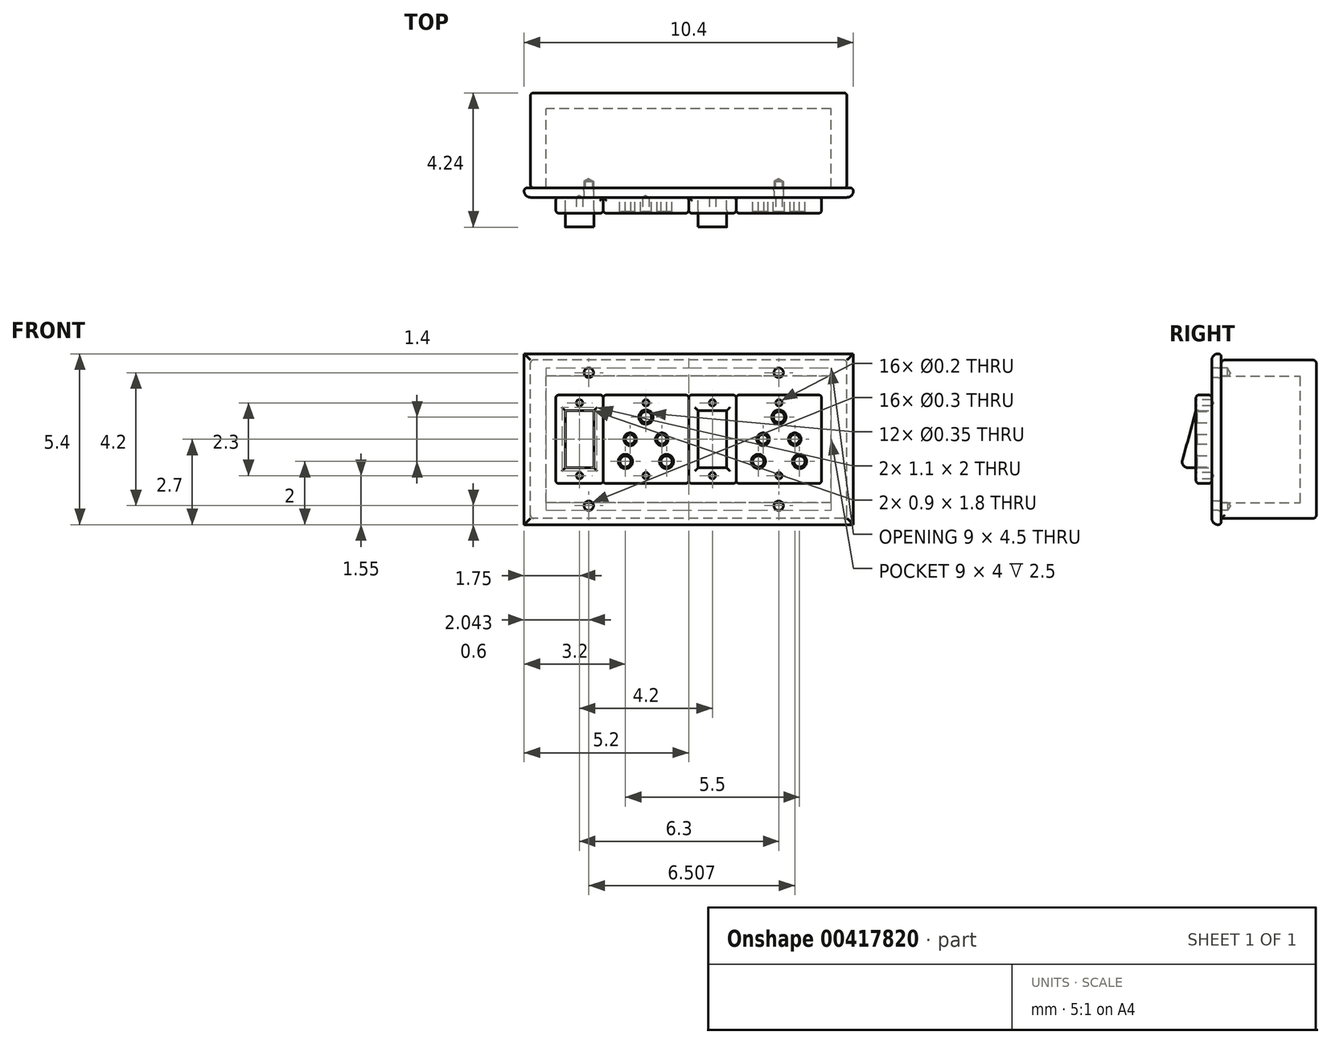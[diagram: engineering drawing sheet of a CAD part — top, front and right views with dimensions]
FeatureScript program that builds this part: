
annotation { "Feature Type Name" : "Feature", "Feature Type Description" : "" }
export const myFeature = defineFeature(function(context is Context, id is Id, definition is map)
    precondition{}
    {
        {
            var Q0;
            Q0=qCreatedBy(makeId("Front.planeOp"),FACE);
            var sketch = newSketch(context, id + "F0", { "sketchPlane" : qUnion([Q0])});
            skLineSegment(sketch, "E0.bottom", {"start": v(5, -2.5) * mm, "end": v(-5, -2.5) * mm});
            skLineSegment(sketch, "E0.top", {"start": v(5, 2.5) * mm, "end": v(-5, 2.5) * mm});
            skLineSegment(sketch, "E0.left", {"start": v(5, -2.5) * mm, "end": v(5, 2.5) * mm});
            skLineSegment(sketch, "E0.right", {"start": v(-5, -2.5) * mm, "end": v(-5, 2.5) * mm});
            skPoint(sketch, "E0.middle", {"position": v(0, 0) * mm});
            skSolve(sketch);
        }
        {
            var Q0;
            Q0=makeQuery(id+"F0.imprint","IMPRINT",FACE,{"disambiguationData":[TD([[makeQuery(id+"F0.imprint","IMPRINT",EDGE,{"derivedFrom":sQuery(id+"F0.wireOp",EDGE,"E0.bottom")}),-1.0]])]});
            extrude(context, id + "F1", {"entities" : qUnion([Q0]), "depth" : 3 * mm});
        }
        {
            var Q0;
            Q0=makeQuery(id+"F1.opExtrude","CAP_FACE",FACE,{"disambiguationData":[OSD([sQuery(id+"F0.wireOp",EDGE,"E0.bottom"),sQuery(id+"F0.wireOp",EDGE,"E0.top"),sQuery(id+"F0.wireOp",EDGE,"E0.left"),sQuery(id+"F0.wireOp",EDGE,"E0.right")])],"isStart":false});
            shell(context, id + "F2", {"entities" : qUnion([Q0]), "thickness" : 0.5 * mm});
        }
        {
            var Q0;
            Q0=makeQuery(id+"F1.opExtrude","CAP_FACE",FACE,{"disambiguationData":[OSD([sQuery(id+"F0.wireOp",EDGE,"E0.bottom"),sQuery(id+"F0.wireOp",EDGE,"E0.top"),sQuery(id+"F0.wireOp",EDGE,"E0.left"),sQuery(id+"F0.wireOp",EDGE,"E0.right")])],"isStart":false});
            var sketch = newSketch(context, id + "F3", { "sketchPlane" : qUnion([Q0])});
            skLineSegment(sketch, "E1.bottom", {"start": v(5.2, -2.7) * mm, "end": v(-5.2, -2.7) * mm});
            skLineSegment(sketch, "E1.top", {"start": v(5.2, 2.7) * mm, "end": v(-5.2, 2.7) * mm});
            skLineSegment(sketch, "E1.left", {"start": v(5.2, -2.7) * mm, "end": v(5.2, 2.7) * mm});
            skLineSegment(sketch, "E1.right", {"start": v(-5.2, -2.7) * mm, "end": v(-5.2, 2.7) * mm});
            skPoint(sketch, "E1.middle", {"position": v(0, 0) * mm});
            skSolve(sketch);
        }
        {
            var Q0;
            Q0=makeQuery(id+"F3.imprint","IMPRINT",FACE,{"disambiguationData":[TD([[makeQuery(id+"F3.imprint","IMPRINT",EDGE,{"derivedFrom":sQuery(id+"F3.wireOp",EDGE,"E1.bottom")}),-1.0]])]});
            var Q1;
            {var subQ0=sQuery(id+"F0.wireOp",EDGE,"E0.bottom");Q1=makeQuery(id+"F3.imprint","IMPRINT",FACE,{"disambiguationData":[TD([[makeQuery(id+"F3.imprint","IMPRINT",EDGE,{"derivedFrom":makeQuery(id+"F2.opShell","OFFSET_EDGE",EDGE,{"disambiguationData":[OSD([subQ0]),TDD([makeQuery(id+"F1.opExtrude","CAP_EDGE",EDGE,{"disambiguationData":[OSD([subQ0])],"isStart":false})])]})}),-1.0]])]});}
            var Q2;
            {var subQ6=sQuery(id+"F0.wireOp",EDGE,"E0.bottom");var subQ7=makeQuery(id+"F1.opExtrude","CAP_EDGE",EDGE,{"disambiguationData":[OSD([subQ6])],"isStart":false});Q2=makeQuery(id+"F3.imprint","IMPRINT",FACE,{"disambiguationData":[TD([[makeQuery(id+"F3.imprint","IMPRINT",EDGE,{"derivedFrom":subQ7}),-1.0]])]});}
            extrude(context, id + "F4", {"entities" : qUnion([Q0, Q1, Q2]), "depth" : 0.3 * mm});
        }
        {
            var Q0;
            Q0=makeQuery(id+"F4.opExtrude","CAP_FACE",FACE,{"disambiguationData":[OSD([sQuery(id+"F3.wireOp",EDGE,"E1.bottom"),sQuery(id+"F3.wireOp",EDGE,"E1.top"),sQuery(id+"F3.wireOp",EDGE,"E1.left"),sQuery(id+"F3.wireOp",EDGE,"E1.right")])],"isStart":false});
            var sketch = newSketch(context, id + "F5", { "sketchPlane" : qUnion([Q0])});
            skLineSegment(sketch, "E2.bottom", {"start": v(-2.7, -1.4) * mm, "end": v(-4.2, -1.4) * mm});
            skLineSegment(sketch, "E2.top", {"start": v(-2.7, 1.4) * mm, "end": v(-4.2, 1.4) * mm});
            skLineSegment(sketch, "E2.left", {"start": v(-2.7, -1.4) * mm, "end": v(-2.7, 1.4) * mm});
            skLineSegment(sketch, "E2.right", {"start": v(-4.2, -1.4) * mm, "end": v(-4.2, 1.4) * mm});
            skPoint(sketch, "E2.middle", {"position": v(-3.45, 0) * mm});
            skLineSegment(sketch, "E3.bottom", {"start": v(0, -1.4) * mm, "end": v(-2.7, -1.4) * mm});
            skLineSegment(sketch, "E3.top", {"start": v(0, 1.4) * mm, "end": v(-2.7, 1.4) * mm});
            skLineSegment(sketch, "E3.left", {"start": v(0, -1.4) * mm, "end": v(0, 1.4) * mm});
            skPoint(sketch, "E3.middle", {"position": v(-1.35, 0) * mm});
            skLineSegment(sketch, "E4.bottom", {"start": v(-3, -0.9) * mm, "end": v(-3.9, -0.9) * mm});
            skLineSegment(sketch, "E4.top", {"start": v(-3, 0.9) * mm, "end": v(-3.9, 0.9) * mm});
            skLineSegment(sketch, "E4.left", {"start": v(-3, -0.9) * mm, "end": v(-3, 0.9) * mm});
            skLineSegment(sketch, "E4.right", {"start": v(-3.9, -0.9) * mm, "end": v(-3.9, 0.9) * mm});
            skCircle(sketch, "E5", {"center": v(-1.35, 0.7) * mm, "radius": 0.17 * mm});
            skCircle(sketch, "E6", {"center": v(-1.85, 0) * mm, "radius": 0.15 * mm});
            skCircle(sketch, "E7", {"center": v(-0.85, 0) * mm, "radius": 0.15 * mm});
            skCircle(sketch, "E8", {"center": v(-2, -0.7) * mm, "radius": 0.17 * mm});
            skCircle(sketch, "E9", {"center": v(-0.7, -0.7) * mm, "radius": 0.17 * mm});
            skPoint(sketch, "E10", {"position": v(-3.45, 1.15) * mm});
            skPoint(sketch, "E11", {"position": v(-1.35, 1.15) * mm});
            skPoint(sketch, "E12", {"position": v(-1.35, -1.15) * mm});
            skPoint(sketch, "E13", {"position": v(-3.45, -1.15) * mm});
            skSolve(sketch);
        }
        {
            var Q0;
            Q0=makeQuery(id+"F5.imprint","IMPRINT",FACE,{"disambiguationData":[TD([[makeQuery(id+"F5.imprint","IMPRINT",EDGE,{"derivedFrom":sQuery(id+"F5.wireOp",EDGE,"E2.bottom")}),-1.0]])]});
            extrude(context, id + "F6", {"entities" : qUnion([Q0]), "depth" : 0.5 * mm});
        }
        {
            var Q0;
            Q0=makeQuery(id+"F5.imprint","IMPRINT",FACE,{"disambiguationData":[TD([[makeQuery(id+"F5.imprint","IMPRINT",EDGE,{"derivedFrom":sQuery(id+"F5.wireOp",EDGE,"E3.bottom")}),-1.0]])]});
            extrude(context, id + "F7", {"entities" : qUnion([Q0]), "depth" : 0.5 * mm});
        }
        {
            var Q0;
            Q0=makeQuery(id+"F6.opExtrude","SWEPT_FACE",FACE,{"disambiguationData":[OSD([sQuery(id+"F5.wireOp",EDGE,"E4.right")])]});
            var sketch = newSketch(context, id + "F8", { "sketchPlane" : qUnion([Q0])});
            skLineSegment(sketch, "E14.0.0", {"start": v(-3.3, -2.7) * mm, "end": v(-3.3, 2.7) * mm});
            skLineSegment(sketch, "E14.0.2", {"start": v(-3.3, 2.7) * mm, "end": v(-3.3, -2.7) * mm});
            skPoint(sketch, "E15.0", {"position": v(-3.8, -0.9) * mm});
            skPoint(sketch, "E16.0", {"position": v(-3.8, 0.9) * mm});
            skLineSegment(sketch, "E17", {"start": v(-3.8, 0.9) * mm, "end": v(-3.8, -0.9) * mm});
            skLineSegment(sketch, "E18", {"start": v(-4.05, -0.9) * mm, "end": v(-3.8, -0.9) * mm});
            skArc(sketch, "E19", {"start": v(-4.23, -0.66) * mm, "mid": v(-4.01, 0.12) * mm, "end": v(-3.8, 0.9) * mm});
            skPoint(sketch, "E20.visualSharp", {"position": v(-4.3, -0.9) * mm});
            skArc(sketch, "E20.filletArc", {"start": v(-4.23, -0.66) * mm, "mid": v(-4.2, -0.82) * mm, "end": v(-4.05, -0.9) * mm});
            skSolve(sketch);
        }
        {
            var Q0;
            Q0=makeQuery(id+"F8.imprint","IMPRINT",FACE,{"disambiguationData":[TD([[makeQuery(id+"F8.imprint","IMPRINT",EDGE,{"derivedFrom":sQuery(id+"F8.wireOp",EDGE,"E17")}),1.0]])]});
            var Q1;
            Q1=makeQuery(id+"F6.opExtrude","SWEPT_FACE",FACE,{"disambiguationData":[OSD([sQuery(id+"F5.wireOp",EDGE,"E4.left")])]});
            extrude(context, id + "F9", {"entities" : qUnion([Q0]), "endBound" : BoundingType.UP_TO_SURFACE, "endBoundEntityFace" : qUnion([Q1]), "depth" : 25 * mm});
        }
        {
            var Q0;
            Q0=makeQuery(id+"F6.opExtrude","CAP_FACE",FACE,{"disambiguationData":[OSD([sQuery(id+"F5.wireOp",EDGE,"E2.bottom"),sQuery(id+"F5.wireOp",EDGE,"E2.top"),sQuery(id+"F5.wireOp",EDGE,"E2.right"),sQuery(id+"F5.wireOp",EDGE,"E2.left"),sQuery(id+"F5.wireOp",EDGE,"E4.bottom"),sQuery(id+"F5.wireOp",EDGE,"E4.top"),sQuery(id+"F5.wireOp",EDGE,"E4.left"),sQuery(id+"F5.wireOp",EDGE,"E4.right")])],"isStart":false});
            var Q1;
            Q1=makeQuery(id+"F6.opExtrude","SWEPT_EDGE",EDGE,{"disambiguationData":[OSD([sQuery(id+"F5.wireOp",EDGE,"E2.top"),sQuery(id+"F5.wireOp",EDGE,"E2.right")])]});
            var Q2;
            Q2=makeQuery(id+"F6.opExtrude","SWEPT_EDGE",EDGE,{"disambiguationData":[OSD([sQuery(id+"F5.wireOp",EDGE,"E2.bottom"),sQuery(id+"F5.wireOp",EDGE,"E2.right")])]});
            var Q3;
            Q3=makeQuery(id+"F6.opExtrude","CAP_EDGE",EDGE,{"disambiguationData":[OSD([sQuery(id+"F5.wireOp",EDGE,"E2.right")])],"isStart":true});
            var Q4;
            Q4=makeQuery(id+"F6.opExtrude","CAP_EDGE",EDGE,{"disambiguationData":[OSD([sQuery(id+"F5.wireOp",EDGE,"E2.top")])],"isStart":true});
            var Q5;
            Q5=makeQuery(id+"F6.opExtrude","CAP_EDGE",EDGE,{"disambiguationData":[OSD([sQuery(id+"F5.wireOp",EDGE,"E2.bottom")])],"isStart":true});
            var Q6;
            Q6=makeQuery(id+"F6.opExtrude","SWEPT_EDGE",EDGE,{"disambiguationData":[OSD([sQuery(id+"F5.wireOp",EDGE,"E2.top"),sQuery(id+"F5.wireOp",EDGE,"E3.top"),sQuery(id+"F5.wireOp",EDGE,"E2.left")])]});
            var Q7;
            Q7=makeQuery(id+"F6.opExtrude","SWEPT_EDGE",EDGE,{"disambiguationData":[OSD([sQuery(id+"F5.wireOp",EDGE,"E2.bottom"),sQuery(id+"F5.wireOp",EDGE,"E3.bottom"),sQuery(id+"F5.wireOp",EDGE,"E2.left")])]});
            fillet(context, id + "F10", {"entities" : qUnion([Q0, Q1, Q2, Q3, Q4, Q5, Q6, Q7]), "radius" : 0.1 * mm, "tangentPropagation" : true, "allowEdgeOverflow" : false});
        }
        {
            var Q0;
            Q0=makeQuery(id+"F7.opExtrude","CAP_EDGE",EDGE,{"disambiguationData":[OSD([sQuery(id+"F5.wireOp",EDGE,"E5")])],"isStart":false});
            var Q1;
            Q1=makeQuery(id+"F7.opExtrude","CAP_EDGE",EDGE,{"disambiguationData":[OSD([sQuery(id+"F5.wireOp",EDGE,"E6")])],"isStart":false});
            var Q2;
            Q2=makeQuery(id+"F7.opExtrude","CAP_EDGE",EDGE,{"disambiguationData":[OSD([sQuery(id+"F5.wireOp",EDGE,"E7")])],"isStart":false});
            var Q3;
            Q3=makeQuery(id+"F7.opExtrude","CAP_EDGE",EDGE,{"disambiguationData":[OSD([sQuery(id+"F5.wireOp",EDGE,"E8")])],"isStart":false});
            var Q4;
            Q4=makeQuery(id+"F7.opExtrude","CAP_EDGE",EDGE,{"disambiguationData":[OSD([sQuery(id+"F5.wireOp",EDGE,"E9")])],"isStart":false});
            chamfer(context, id + "F11", {"entities" : qUnion([Q0, Q1, Q2, Q3, Q4]), "width" : 0.05 * mm, "tangentPropagation" : true});
        }
        {
            var Q0;
            Q0=makeQuery(id+"F7.opExtrude","SWEPT_FACE",FACE,{"disambiguationData":[OSD([sQuery(id+"F5.wireOp",EDGE,"E3.top")])]});
            var Q1;
            Q1=makeQuery(id+"F7.opExtrude","SWEPT_FACE",FACE,{"disambiguationData":[OSD([sQuery(id+"F5.wireOp",EDGE,"E3.left")])]});
            var Q2;
            Q2=makeQuery(id+"F7.opExtrude","SWEPT_FACE",FACE,{"disambiguationData":[OSD([sQuery(id+"F5.wireOp",EDGE,"E3.bottom")])]});
            fillet(context, id + "F12", {"entities" : qUnion([Q0, Q1, Q2]), "radius" : 0.1 * mm, "tangentPropagation" : true, "allowEdgeOverflow" : false});
        }
        {
            var Q0;
            Q0=makeQuery(id+"F4.opExtrude","CAP_FACE",FACE,{"disambiguationData":[OSD([sQuery(id+"F3.wireOp",EDGE,"E1.bottom"),sQuery(id+"F3.wireOp",EDGE,"E1.top"),sQuery(id+"F3.wireOp",EDGE,"E1.left"),sQuery(id+"F3.wireOp",EDGE,"E1.right")])],"isStart":false});
            fillet(context, id + "F13", {"entities" : qUnion([Q0]), "radius" : 0.2 * mm, "tangentPropagation" : true, "allowEdgeOverflow" : false});
        }
        {
            var Q0;
            Q0=makeQuery(id+"F6.opExtrude","CAP_FACE",FACE,{"disambiguationData":[OSD([sQuery(id+"F5.wireOp",EDGE,"E2.bottom"),sQuery(id+"F5.wireOp",EDGE,"E2.top"),sQuery(id+"F5.wireOp",EDGE,"E2.right"),sQuery(id+"F5.wireOp",EDGE,"E2.left"),sQuery(id+"F5.wireOp",EDGE,"E4.bottom"),sQuery(id+"F5.wireOp",EDGE,"E4.top"),sQuery(id+"F5.wireOp",EDGE,"E4.left"),sQuery(id+"F5.wireOp",EDGE,"E4.right")])],"isStart":false});
            var sketch = newSketch(context, id + "F14", { "sketchPlane" : qUnion([Q0])});
            skPoint(sketch, "E21.0", {"position": v(-3.45, 1.15) * mm});
            skPoint(sketch, "E22.0", {"position": v(-3.45, -1.15) * mm});
            skPoint(sketch, "E23.0", {"position": v(-1.35, 1.15) * mm});
            skPoint(sketch, "E24.0", {"position": v(-1.35, -1.15) * mm});
            skSolve(sketch);
        }
        {
            var Q0;
            Q0=sQuery(id+"F14.wireOp",VERTEX,"E21.0");
            var Q1;
            Q1=sQuery(id+"F14.wireOp",VERTEX,"E23.0");
            var Q2;
            Q2=sQuery(id+"F14.wireOp",VERTEX,"E22.0");
            var Q3;
            Q3=sQuery(id+"F14.wireOp",VERTEX,"E24.0");
            var Q4;
            Q4=makeQuery(id+"F4.opExtrude","SWEPT_BODY",BODY,{"disambiguationData":[OSD([sQuery(id+"F3.wireOp",EDGE,"E1.bottom"),sQuery(id+"F3.wireOp",EDGE,"E1.top"),sQuery(id+"F3.wireOp",EDGE,"E1.left"),sQuery(id+"F3.wireOp",EDGE,"E1.right")])]});
            var Q5;
            Q5=makeQuery(id+"F6.opExtrude","SWEPT_BODY",BODY,{"disambiguationData":[OSD([sQuery(id+"F5.wireOp",EDGE,"E2.bottom"),sQuery(id+"F5.wireOp",EDGE,"E2.top"),sQuery(id+"F5.wireOp",EDGE,"E2.right"),sQuery(id+"F5.wireOp",EDGE,"E2.left"),sQuery(id+"F5.wireOp",EDGE,"E4.bottom"),sQuery(id+"F5.wireOp",EDGE,"E4.top"),sQuery(id+"F5.wireOp",EDGE,"E4.left"),sQuery(id+"F5.wireOp",EDGE,"E4.right")])]});
            var Q6;
            Q6=makeQuery(id+"F7.opExtrude","SWEPT_BODY",BODY,{"disambiguationData":[OSD([sQuery(id+"F5.wireOp",EDGE,"E3.bottom"),sQuery(id+"F5.wireOp",EDGE,"E3.top"),sQuery(id+"F5.wireOp",EDGE,"E3.left"),sQuery(id+"F5.wireOp",EDGE,"E2.left"),sQuery(id+"F5.wireOp",EDGE,"E5"),sQuery(id+"F5.wireOp",EDGE,"E6"),sQuery(id+"F5.wireOp",EDGE,"E7"),sQuery(id+"F5.wireOp",EDGE,"E8"),sQuery(id+"F5.wireOp",EDGE,"E9")])]});
            hole(context, id + "F15", {"style" : HoleStyle.SIMPLE, "endStyle" : HoleEndStyle.BLIND, "holeDiameter" : 0.2 * mm, "holeDepth" : 0.5 * mm, "isTappedThrough" : true, "tappedDepth" : 19.25 * mm, "tapClearance" : 3, "startFromSketch" : true, "locations" : qUnion([Q0, Q1, Q2, Q3]), "scope" : qUnion([Q4, Q5, Q6])});
        }
        {
            var Q0;
            Q0=makeQuery(id+"F4.opExtrude","CAP_FACE",FACE,{"disambiguationData":[OSD([sQuery(id+"F3.wireOp",EDGE,"E1.bottom"),sQuery(id+"F3.wireOp",EDGE,"E1.top"),sQuery(id+"F3.wireOp",EDGE,"E1.left"),sQuery(id+"F3.wireOp",EDGE,"E1.right")])],"isStart":false});
            var sketch = newSketch(context, id + "F16", { "sketchPlane" : qUnion([Q0])});
            skPoint(sketch, "E25", {"position": v(-3.16, 2.1) * mm});
            skPoint(sketch, "E26", {"position": v(2.84, 2.1) * mm});
            skPoint(sketch, "E27", {"position": v(-3.16, -2.1) * mm});
            skPoint(sketch, "E28", {"position": v(2.84, -2.1) * mm});
            skSolve(sketch);
        }
        {
            var Q0;
            Q0=sQuery(id+"F16.wireOp",VERTEX,"E25");
            var Q1;
            Q1=sQuery(id+"F16.wireOp",VERTEX,"E26");
            var Q2;
            Q2=sQuery(id+"F16.wireOp",VERTEX,"E27");
            var Q3;
            Q3=sQuery(id+"F16.wireOp",VERTEX,"E28");
            var Q4;
            Q4=makeQuery(id+"F4.opExtrude","SWEPT_BODY",BODY,{"disambiguationData":[OSD([sQuery(id+"F3.wireOp",EDGE,"E1.bottom"),sQuery(id+"F3.wireOp",EDGE,"E1.top"),sQuery(id+"F3.wireOp",EDGE,"E1.left"),sQuery(id+"F3.wireOp",EDGE,"E1.right")])]});
            var Q5;
            Q5=makeQuery(id+"F1.opExtrude","SWEPT_BODY",BODY,{"disambiguationData":[OSD([sQuery(id+"F0.wireOp",EDGE,"E0.bottom"),sQuery(id+"F0.wireOp",EDGE,"E0.top"),sQuery(id+"F0.wireOp",EDGE,"E0.left"),sQuery(id+"F0.wireOp",EDGE,"E0.right")])]});
            hole(context, id + "F17", {"style" : HoleStyle.SIMPLE, "endStyle" : HoleEndStyle.BLIND, "holeDiameter" : 0.3 * mm, "holeDepth" : 0.5 * mm, "isTappedThrough" : true, "tappedDepth" : 19.25 * mm, "tapClearance" : 3, "startFromSketch" : true, "locations" : qUnion([Q0, Q1, Q2, Q3]), "scope" : qUnion([Q4, Q5])});
        }
        {
            var Q0;
            Q0=qCreatedBy(makeId("Right.planeOp"),FACE);
            cPlane(context, id + "F18", {"entities" : qUnion([Q0]), "cplaneType" : CPlaneType.OFFSET, "offset" : (2.7 / 2) * mm, "oppositeDirection" : true, "width" : 150 * mm, "height" : 150 * mm});
        }
        {
            var Q0;
            Q0=makeQuery(id+"F6.opExtrude","SWEPT_BODY",BODY,{"disambiguationData":[OSD([sQuery(id+"F5.wireOp",EDGE,"E2.bottom"),sQuery(id+"F5.wireOp",EDGE,"E2.top"),sQuery(id+"F5.wireOp",EDGE,"E2.right"),sQuery(id+"F5.wireOp",EDGE,"E2.left"),sQuery(id+"F5.wireOp",EDGE,"E4.bottom"),sQuery(id+"F5.wireOp",EDGE,"E4.top"),sQuery(id+"F5.wireOp",EDGE,"E4.left"),sQuery(id+"F5.wireOp",EDGE,"E4.right")])]});
            var Q1;
            Q1=makeQuery(id+"F9.opExtrude","SWEPT_BODY",BODY,{"disambiguationData":[OSD([sQuery(id+"F8.wireOp",EDGE,"E17"),sQuery(id+"F8.wireOp",EDGE,"E18"),sQuery(id+"F8.wireOp",EDGE,"E19"),sQuery(id+"F8.wireOp",EDGE,"E20.filletArc")])]});
            var Q2;
            Q2=qCreatedBy(id+"F18.planeOp",FACE);
            mirror(context, id + "F19", {"entities" : qUnion([Q0, Q1]), "mirrorPlane" : qUnion([Q2])});
        }
        {
            var Q0;
            Q0=qCreatedBy(makeId("Right.planeOp"),FACE);
            cPlane(context, id + "F20", {"entities" : qUnion([Q0]), "cplaneType" : CPlaneType.OFFSET, "offset" : (1.5 / 2) * mm, "width" : 150 * mm, "height" : 150 * mm});
        }
        {
            var Q0;
            Q0=makeQuery(id+"F7.opExtrude","SWEPT_BODY",BODY,{"disambiguationData":[OSD([sQuery(id+"F5.wireOp",EDGE,"E3.bottom"),sQuery(id+"F5.wireOp",EDGE,"E3.top"),sQuery(id+"F5.wireOp",EDGE,"E3.left"),sQuery(id+"F5.wireOp",EDGE,"E2.left"),sQuery(id+"F5.wireOp",EDGE,"E5"),sQuery(id+"F5.wireOp",EDGE,"E6"),sQuery(id+"F5.wireOp",EDGE,"E7"),sQuery(id+"F5.wireOp",EDGE,"E8"),sQuery(id+"F5.wireOp",EDGE,"E9")])]});
            var Q1;
            Q1=qCreatedBy(id+"F20.planeOp",FACE);
            mirror(context, id + "F21", {"entities" : qUnion([Q0]), "mirrorPlane" : qUnion([Q1])});
        }
        {
            var Q0;
            Q0=makeQuery(id+"F21.opPattern","COPY",FACE,{"derivedFrom":makeQuery(id+"F7.opExtrude","SWEPT_FACE",FACE,{"disambiguationData":[OSD([sQuery(id+"F5.wireOp",EDGE,"E2.left")])]}),"instanceName":"1"});
            var Q1;
            Q1=makeQuery(id+"F7.opExtrude","CAP_EDGE",EDGE,{"disambiguationData":[OSD([sQuery(id+"F5.wireOp",EDGE,"E2.left")])],"isStart":false});
            fillet(context, id + "F22", {"entities" : qUnion([Q0, Q1]), "radius" : 0.1 * mm, "tangentPropagation" : true, "allowEdgeOverflow" : false});
        }
        {
            var Q0;
            Q0=makeQuery(id+"F4.opExtrude","CAP_FACE",FACE,{"disambiguationData":[OSD([sQuery(id+"F3.wireOp",EDGE,"E1.bottom"),sQuery(id+"F3.wireOp",EDGE,"E1.top"),sQuery(id+"F3.wireOp",EDGE,"E1.left"),sQuery(id+"F3.wireOp",EDGE,"E1.right")])],"isStart":true});
            var Q1;
            Q1=makeQuery(id+"F1.opExtrude","SWEPT_FACE",FACE,{"disambiguationData":[OSD([sQuery(id+"F0.wireOp",EDGE,"E0.left")])]});
            var Q2;
            Q2=makeQuery(id+"F1.opExtrude","SWEPT_FACE",FACE,{"disambiguationData":[OSD([sQuery(id+"F0.wireOp",EDGE,"E0.top")])]});
            var Q3;
            Q3=makeQuery(id+"F1.opExtrude","CAP_FACE",FACE,{"disambiguationData":[OSD([sQuery(id+"F0.wireOp",EDGE,"E0.bottom"),sQuery(id+"F0.wireOp",EDGE,"E0.top"),sQuery(id+"F0.wireOp",EDGE,"E0.left"),sQuery(id+"F0.wireOp",EDGE,"E0.right")])],"isStart":true});
            var Q4;
            Q4=makeQuery(id+"F1.opExtrude","SWEPT_FACE",FACE,{"disambiguationData":[OSD([sQuery(id+"F0.wireOp",EDGE,"E0.right")])]});
            fillet(context, id + "F23", {"entities" : qUnion([Q0, Q1, Q2, Q3, Q4]), "radius" : 0.1 * mm, "tangentPropagation" : true, "allowEdgeOverflow" : false});
        }
    });
